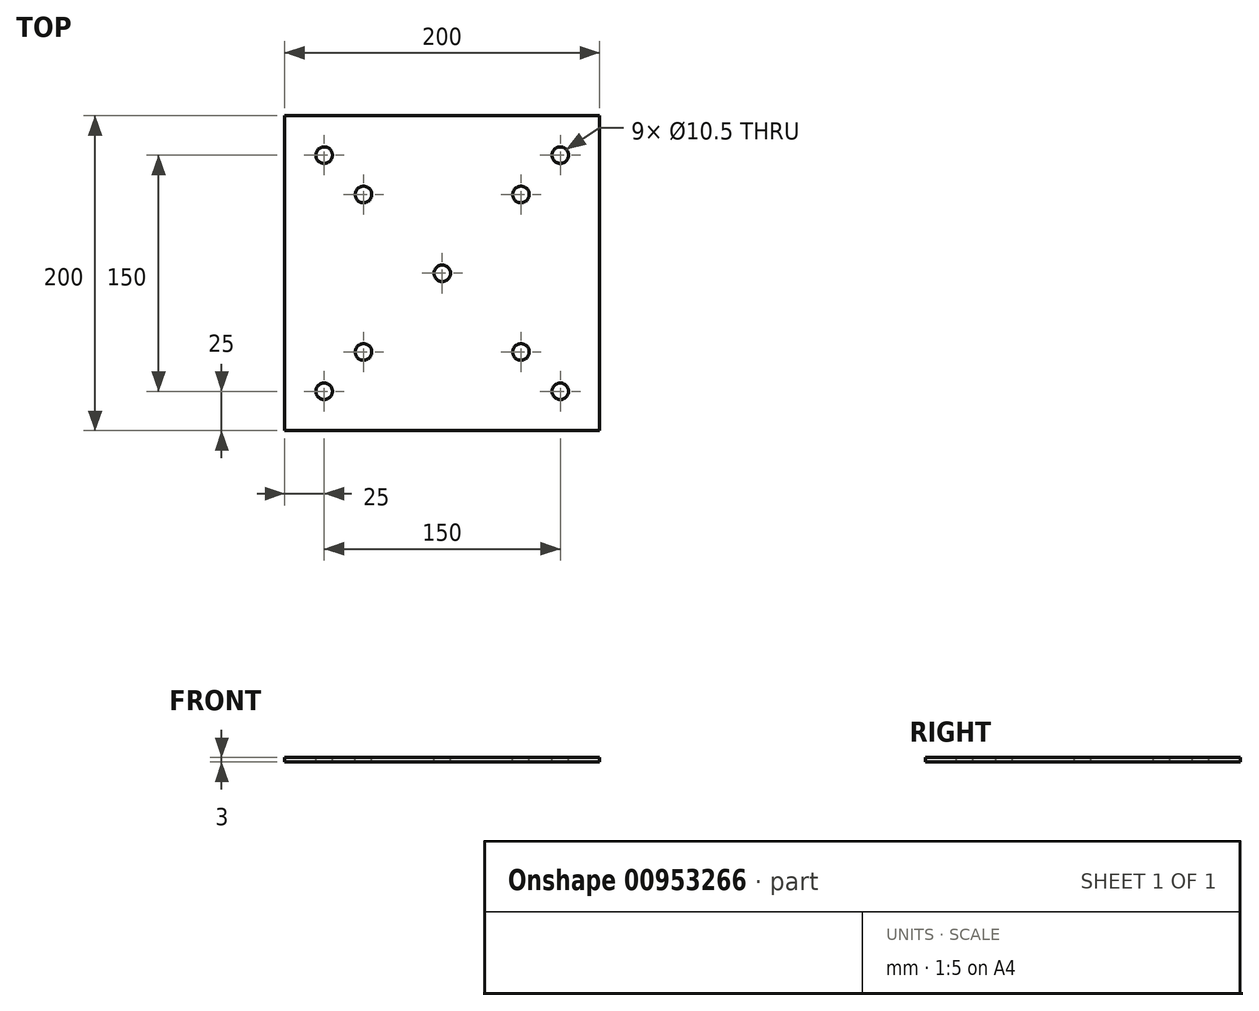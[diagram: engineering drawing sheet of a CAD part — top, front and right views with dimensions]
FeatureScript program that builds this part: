
annotation { "Feature Type Name" : "Feature", "Feature Type Description" : "" }
export const myFeature = defineFeature(function(context is Context, id is Id, definition is map)
    precondition{}
    {
        {
            var Q0;
            Q0=qCreatedBy(makeId("Top.planeOp"),FACE);
            var sketch = newSketch(context, id + "F0", { "sketchPlane" : qUnion([Q0])});
            skLineSegment(sketch, "E0.bottom", {"start": v(100, 100) * mm, "end": v(-100, 100) * mm});
            skLineSegment(sketch, "E0.top", {"start": v(100, -100) * mm, "end": v(-100, -100) * mm});
            skLineSegment(sketch, "E0.left", {"start": v(100, 100) * mm, "end": v(100, -100) * mm});
            skLineSegment(sketch, "E0.right", {"start": v(-100, 100) * mm, "end": v(-100, -100) * mm});
            skPoint(sketch, "E0.middle", {"position": v(0, 0) * mm});
            skSolve(sketch);
        }
        {
            var Q0;
            Q0=makeQuery(id+"F0.imprint","IMPRINT",FACE,{"disambiguationData":[TD([[makeQuery(id+"F0.imprint","IMPRINT",EDGE,{"derivedFrom":sQuery(id+"F0.wireOp",EDGE,"E0.bottom")}),1.0]])]});
            extrude(context, id + "F1", {"entities" : qUnion([Q0]), "depth" : 3 * mm, "offsetDistance" : 25 * mm});
        }
        {
            var Q0;
            Q0=makeQuery(id+"F1.opExtrude","CAP_FACE",FACE,{"disambiguationData":[OSD([sQuery(id+"F0.wireOp",EDGE,"E0.bottom"),sQuery(id+"F0.wireOp",EDGE,"E0.top"),sQuery(id+"F0.wireOp",EDGE,"E0.left"),sQuery(id+"F0.wireOp",EDGE,"E0.right")])],"isStart":false});
            var sketch = newSketch(context, id + "F2", { "sketchPlane" : qUnion([Q0])});
            skLineSegment(sketch, "E1.bottom", {"start": v(50, 50) * mm, "end": v(-50, 50) * mm});
            skLineSegment(sketch, "E1.top", {"start": v(50, -50) * mm, "end": v(-50, -50) * mm});
            skLineSegment(sketch, "E1.left", {"start": v(50, 50) * mm, "end": v(50, -50) * mm});
            skLineSegment(sketch, "E1.right", {"start": v(-50, 50) * mm, "end": v(-50, -50) * mm});
            skPoint(sketch, "E1.middle", {"position": v(0, 0) * mm});
            skLineSegment(sketch, "E2.bottom", {"start": v(75, 75) * mm, "end": v(-75, 75) * mm});
            skLineSegment(sketch, "E2.top", {"start": v(75, -75) * mm, "end": v(-75, -75) * mm});
            skLineSegment(sketch, "E2.left", {"start": v(75, 75) * mm, "end": v(75, -75) * mm});
            skLineSegment(sketch, "E2.right", {"start": v(-75, 75) * mm, "end": v(-75, -75) * mm});
            skPoint(sketch, "E3", {"position": v(-75, 75) * mm});
            skPoint(sketch, "E4", {"position": v(75, 75) * mm});
            skPoint(sketch, "E5", {"position": v(-50, 50) * mm});
            skPoint(sketch, "E6", {"position": v(-50, -50) * mm});
            skPoint(sketch, "E7", {"position": v(50, -50) * mm});
            skPoint(sketch, "E8", {"position": v(50, 50) * mm});
            skSolve(sketch);
        }
        {
            var Q0;
            Q0=sQuery(id+"F2.wireOp",VERTEX,"E2.bottom.start");
            var Q1;
            Q1=sQuery(id+"F2.wireOp",VERTEX,"E1.left.start");
            var Q2;
            Q2=sQuery(id+"F2.wireOp",VERTEX,"E3");
            var Q3;
            Q3=sQuery(id+"F2.wireOp",VERTEX,"E5");
            var Q4;
            Q4=sQuery(id+"F2.wireOp",VERTEX,"E1.right.end");
            var Q5;
            Q5=sQuery(id+"F2.wireOp",VERTEX,"E2.top.end");
            var Q6;
            Q6=sQuery(id+"F2.wireOp",VERTEX,"E1.left.end");
            var Q7;
            Q7=sQuery(id+"F2.wireOp",VERTEX,"E2.top.start");
            var Q8;
            Q8=sQuery(id+"F2.wireOp",VERTEX,"E1.middle");
            var Q9;
            Q9=makeQuery(id+"F1.opExtrude","SWEPT_BODY",BODY,{"disambiguationData":[OSD([sQuery(id+"F0.wireOp",EDGE,"E0.bottom"),sQuery(id+"F0.wireOp",EDGE,"E0.top"),sQuery(id+"F0.wireOp",EDGE,"E0.left"),sQuery(id+"F0.wireOp",EDGE,"E0.right")])]});
            hole(context, id + "F3", {"style" : HoleStyle.SIMPLE, "endStyle" : HoleEndStyle.THROUGH, "standardTappedOrClearance" : lookupTablePath({ "standard" : "ISO", "fit" : "Close", "size" : "M10", "type" : "Clearance" }), "standardBlindInLast" : lookupTablePath({ "fit" : "Close", "standard" : "ISO", "engagement" : "75%", "pitch" : "1.5 mm", "size" : "M10", "type" : "Clearance & tapped" }), "holeDiameter" : 10.5 * mm, "majorDiameter" : 5 * mm, "isTappedThrough" : true, "tappedDepth" : 12 * mm, "tapClearance" : 3, "locations" : qUnion([Q0, Q1, Q2, Q3, Q4, Q5, Q6, Q7, Q8]), "scope" : qUnion([Q9])});
        }
    });
